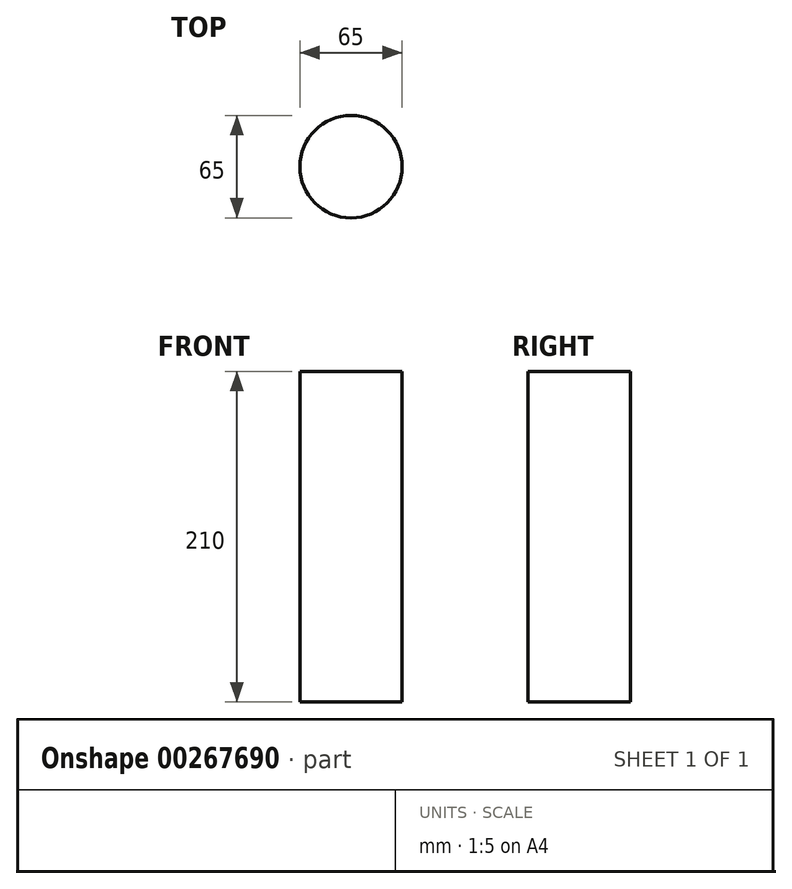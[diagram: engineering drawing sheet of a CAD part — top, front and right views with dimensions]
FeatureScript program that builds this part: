
annotation { "Feature Type Name" : "Feature", "Feature Type Description" : "" }
export const myFeature = defineFeature(function(context is Context, id is Id, definition is map)
    precondition{}
    {
        {
            var Q0;
            Q0=qCreatedBy(makeId("Top.planeOp"),FACE);
            var sketch = newSketch(context, id + "F0", { "sketchPlane" : qUnion([Q0])});
            skCircle(sketch, "E0", {"center": v(0, 0) * mm, "radius": 32.5 * mm});
            skSolve(sketch);
        }
        {
            var Q0;
            Q0=makeQuery(id+"F0.imprint","IMPRINT",FACE,{"disambiguationData":[TD([[makeQuery(id+"F0.imprint","IMPRINT",EDGE,{"derivedFrom":sQuery(id+"F0.wireOp",EDGE,"E0")}),1.0]])]});
            extrude(context, id + "F1", {"entities" : qUnion([Q0]), "oppositeDirection" : true, "depth" : 210 * mm});
        }
    });
